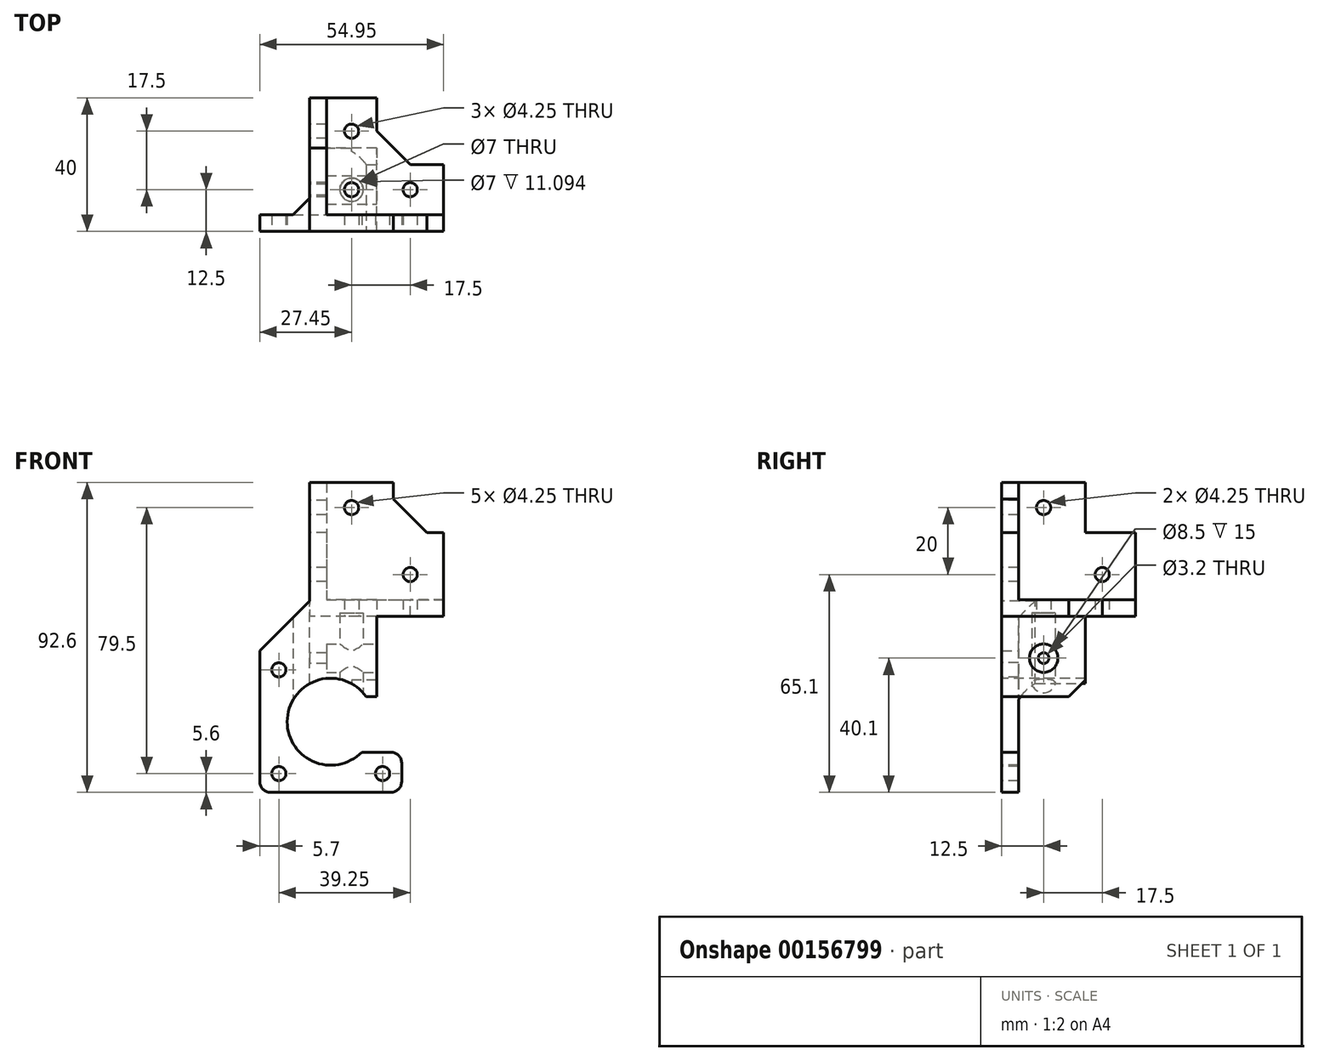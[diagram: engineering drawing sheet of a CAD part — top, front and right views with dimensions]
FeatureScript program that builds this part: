
annotation { "Feature Type Name" : "Feature", "Feature Type Description" : "" }
export const myFeature = defineFeature(function(context is Context, id is Id, definition is map)
    precondition{}
    {
        {
            var Q0;
            Q0=qCreatedBy(makeId("Top.planeOp"),FACE);
            var sketch = newSketch(context, id + "F0", { "sketchPlane" : qUnion([Q0])});
            skLineSegment(sketch, "E0", {"start": v(0, 40) * mm, "end": v(-20, 40) * mm});
            skLineSegment(sketch, "E1", {"start": v(-20, 40) * mm, "end": v(-20, 0) * mm});
            skLineSegment(sketch, "E2", {"start": v(-20, 0) * mm, "end": v(20, 0) * mm});
            skLineSegment(sketch, "E3", {"start": v(20, 0) * mm, "end": v(20, 20) * mm});
            skLineSegment(sketch, "E4", {"start": v(20, 20) * mm, "end": v(0, 20) * mm});
            skLineSegment(sketch, "E5", {"start": v(0, 20) * mm, "end": v(0, 40) * mm});
            skCircle(sketch, "E6", {"center": v(-7.5, 30) * mm, "radius": 2.12 * mm});
            skCircle(sketch, "E7", {"center": v(10, 12.5) * mm, "radius": 2.12 * mm});
            skCircle(sketch, "E8", {"center": v(-7.5, 12.5) * mm, "radius": 2.12 * mm});
            skSolve(sketch);
        }
        {
            var Q0;
            Q0=qSketchRegion(id+"F0",true);
            extrude(context, id + "F1", {"entities" : qUnion([Q0]), "depth" : 5 * mm});
        }
        {
            var Q0;
            Q0=makeQuery(id+"F1.opExtrude","CAP_FACE",FACE,{"disambiguationData":[OSD([sQuery(id+"F0.wireOp",EDGE,"E0"),sQuery(id+"F0.wireOp",EDGE,"E1"),sQuery(id+"F0.wireOp",EDGE,"E2"),sQuery(id+"F0.wireOp",EDGE,"E3"),sQuery(id+"F0.wireOp",EDGE,"E4"),sQuery(id+"F0.wireOp",EDGE,"E5"),sQuery(id+"F0.wireOp",EDGE,"E6"),sQuery(id+"F0.wireOp",EDGE,"E7")])],"isStart":false});
            var sketch = newSketch(context, id + "F2", { "sketchPlane" : qUnion([Q0])});
            skLineSegment(sketch, "E9", {"start": v(-20, 40) * mm, "end": v(-15, 40) * mm});
            skLineSegment(sketch, "E10", {"start": v(-15, 40) * mm, "end": v(-15, 5) * mm});
            skLineSegment(sketch, "E11", {"start": v(-15, 5) * mm, "end": v(20, 5) * mm});
            skLineSegment(sketch, "E12", {"start": v(20, 5) * mm, "end": v(20, 0) * mm});
            skLineSegment(sketch, "E13", {"start": v(20, 0) * mm, "end": v(-20, 0) * mm});
            skLineSegment(sketch, "E14", {"start": v(-20, 0) * mm, "end": v(-20, 40) * mm});
            skSolve(sketch);
        }
        {
            var Q0;
            Q0=qSketchRegion(id+"F2",true);
            extrude(context, id + "F3", {"entities" : qUnion([Q0]), "operationType" : NewBodyOperationType.ADD, "depth" : 20 * mm});
        }
        {
            var Q0;
            Q0=makeQuery(id+"F3.opExtrude","CAP_FACE",FACE,{"disambiguationData":[OSD([sQuery(id+"F2.wireOp",EDGE,"E9"),sQuery(id+"F2.wireOp",EDGE,"E10"),sQuery(id+"F2.wireOp",EDGE,"E11"),sQuery(id+"F2.wireOp",EDGE,"E12"),sQuery(id+"F2.wireOp",EDGE,"E13"),sQuery(id+"F2.wireOp",EDGE,"E14")])],"isStart":false});
            var sketch = newSketch(context, id + "F4", { "sketchPlane" : qUnion([Q0])});
            skLineSegment(sketch, "E15", {"start": v(-15, 25) * mm, "end": v(-20, 25) * mm});
            skLineSegment(sketch, "E16", {"start": v(-20, 25) * mm, "end": v(-20, 0) * mm});
            skLineSegment(sketch, "E17", {"start": v(-20, 0) * mm, "end": v(5, 0) * mm});
            skLineSegment(sketch, "E18", {"start": v(5, 0) * mm, "end": v(5, 5) * mm});
            skLineSegment(sketch, "E19", {"start": v(5, 5) * mm, "end": v(-15, 5) * mm});
            skLineSegment(sketch, "E20", {"start": v(-15, 5) * mm, "end": v(-15, 25) * mm});
            skSolve(sketch);
        }
        {
            var Q0;
            Q0=qSketchRegion(id+"F4",true);
            extrude(context, id + "F5", {"entities" : qUnion([Q0]), "operationType" : NewBodyOperationType.ADD, "depth" : 15 * mm});
        }
        {
            var Q0;
            Q0=makeQuery(id+"F1.opExtrude","SWEPT_EDGE",EDGE,{"disambiguationData":[OSD([sQuery(id+"F0.wireOp",EDGE,"E4"),sQuery(id+"F0.wireOp",EDGE,"E5")])]});
            var Q1;
            Q1=makeQuery(id+"F5.opExtrude","CAP_EDGE",EDGE,{"disambiguationData":[OSD([sQuery(id+"F4.wireOp",EDGE,"E15")])],"isStart":true});
            var Q2;
            Q2=makeQuery(id+"F5.opExtrude","CAP_EDGE",EDGE,{"disambiguationData":[OSD([sQuery(id+"F4.wireOp",EDGE,"E18")])],"isStart":true});
            chamfer(context, id + "F6", {"entities" : qUnion([Q0, Q1, Q2]), "width" : 10 * mm, "tangentPropagation" : true});
        }
        {
            var Q0;
            Q0=makeQuery(id+"F5.boolean.opBoolean","MERGE",FACE,{"derivedFrom":[makeQuery(id+"F3.boolean.opBoolean","MERGE",FACE,{"derivedFrom":[makeQuery(id+"F1.opExtrude","SWEPT_FACE",FACE,{"disambiguationData":[OSD([sQuery(id+"F0.wireOp",EDGE,"E2")])]}),makeQuery(id+"F3.opExtrude","SWEPT_FACE",FACE,{"disambiguationData":[OSD([sQuery(id+"F2.wireOp",EDGE,"E13")])]})]}),makeQuery(id+"F5.opExtrude","SWEPT_FACE",FACE,{"disambiguationData":[OSD([sQuery(id+"F4.wireOp",EDGE,"E17")])]})]});
            var sketch = newSketch(context, id + "F7", { "sketchPlane" : qUnion([Q0])});
            skCircle(sketch, "E21", {"center": v(-7.5, 32.5) * mm, "radius": 2.12 * mm});
            skCircle(sketch, "E22", {"center": v(10, 12.5) * mm, "radius": 2.12 * mm});
            skSolve(sketch);
        }
        {
            var Q0;
            Q0=qSketchRegion(id+"F7",true);
            extrude(context, id + "F8", {"entities" : qUnion([Q0]), "operationType" : NewBodyOperationType.REMOVE, "oppositeDirection" : true, "depth" : 5 * mm});
        }
        {
            var Q0;
            Q0=makeQuery(id+"F5.boolean.opBoolean","MERGE",FACE,{"derivedFrom":[makeQuery(id+"F3.boolean.opBoolean","MERGE",FACE,{"derivedFrom":[makeQuery(id+"F1.opExtrude","SWEPT_FACE",FACE,{"disambiguationData":[OSD([sQuery(id+"F0.wireOp",EDGE,"E1")])]}),makeQuery(id+"F3.opExtrude","SWEPT_FACE",FACE,{"disambiguationData":[OSD([sQuery(id+"F2.wireOp",EDGE,"E14")])]})]}),makeQuery(id+"F5.opExtrude","SWEPT_FACE",FACE,{"disambiguationData":[OSD([sQuery(id+"F4.wireOp",EDGE,"E16")])]})]});
            var sketch = newSketch(context, id + "F9", { "sketchPlane" : qUnion([Q0])});
            skCircle(sketch, "E23", {"center": v(-12.5, 32.5) * mm, "radius": 2.12 * mm});
            skCircle(sketch, "E24", {"center": v(-30, 12.5) * mm, "radius": 2.12 * mm});
            skSolve(sketch);
        }
        {
            var Q0;
            Q0=qSketchRegion(id+"F9",true);
            extrude(context, id + "F10", {"entities" : qUnion([Q0]), "operationType" : NewBodyOperationType.REMOVE, "oppositeDirection" : true, "depth" : 5 * mm});
        }
        {
            var Q0;
            Q0=makeQuery(id+"F1.opExtrude","CAP_FACE",FACE,{"disambiguationData":[OSD([sQuery(id+"F0.wireOp",EDGE,"E0"),sQuery(id+"F0.wireOp",EDGE,"E1"),sQuery(id+"F0.wireOp",EDGE,"E2"),sQuery(id+"F0.wireOp",EDGE,"E3"),sQuery(id+"F0.wireOp",EDGE,"E4"),sQuery(id+"F0.wireOp",EDGE,"E5"),sQuery(id+"F0.wireOp",EDGE,"E6"),sQuery(id+"F0.wireOp",EDGE,"E7"),sQuery(id+"F0.wireOp",EDGE,"E8")])],"isStart":true});
            var sketch = newSketch(context, id + "F11", { "sketchPlane" : qUnion([Q0])});
            skLineSegment(sketch, "E25.bottom", {"start": v(20, -20) * mm, "end": v(-20, -20) * mm});
            skLineSegment(sketch, "E25.top", {"start": v(20, 0) * mm, "end": v(-20, 0) * mm});
            skLineSegment(sketch, "E25.left", {"start": v(20, -20) * mm, "end": v(20, 0) * mm});
            skLineSegment(sketch, "E25.right", {"start": v(-20, -20) * mm, "end": v(-20, 0) * mm});
            skPoint(sketch, "E25.middle", {"position": v(0, -10) * mm});
            skPoint(sketch, "E26.visualSharp", {"position": v(-20, 0) * mm});
            skLineSegment(sketch, "E26.filletArc", {"start": v(-20, 0) * mm, "end": v(-20, 0) * mm});
            skCircle(sketch, "E27", {"center": v(10, -12.5) * mm, "radius": 2.12 * mm});
            skCircle(sketch, "E28", {"center": v(-7.5, -12.5) * mm, "radius": 2.12 * mm});
            skSolve(sketch);
        }
        {
            var Q0;
            Q0=qSketchRegion(id+"F11",true);
            extrude(context, id + "F12", {"entities" : qUnion([Q0]), "operationType" : NewBodyOperationType.ADD, "depth" : 24 * mm});
        }
        {
            var Q0;
            Q0=makeQuery(id+"F12.boolean.opBoolean","MERGE",FACE,{"derivedFrom":[makeQuery(id+"F1.opExtrude","SWEPT_FACE",FACE,{"disambiguationData":[OSD([sQuery(id+"F0.wireOp",EDGE,"E4")])]}),makeQuery(id+"F12.opExtrude","SWEPT_FACE",FACE,{"disambiguationData":[OSD([sQuery(id+"F11.wireOp",EDGE,"E25.bottom")])]})]});
            var sketch = newSketch(context, id + "F13", { "sketchPlane" : qUnion([Q0])});
            skLineSegment(sketch, "E29", {"start": v(20, -11.5) * mm, "end": v(20, -24) * mm});
            skLineSegment(sketch, "E30", {"start": v(20, -24) * mm, "end": v(7.5, -24) * mm});
            skPoint(sketch, "E31.orphan", {"position": v(7.5, -24) * mm});
            skCircle(sketch, "E32", {"center": v(7.5, -11.5) * mm, "radius": 4.15 * mm, "construction": true});
            skLineSegment(sketch, "E33", {"start": v(0, -11.5) * mm, "end": v(0, 0) * mm});
            skLineSegment(sketch, "E34", {"start": v(0, 0) * mm, "end": v(-20, 0) * mm});
            skLineSegment(sketch, "E35", {"start": v(-20, 0) * mm, "end": v(-20, -24) * mm});
            skLineSegment(sketch, "E36", {"start": v(-20, -24) * mm, "end": v(7.5, -24) * mm});
            skLineSegment(sketch, "E37", {"start": v(0, -11.5) * mm, "end": v(0, -24) * mm});
            skSolve(sketch);
        }
        {
            var Q0;
            Q0=qSketchRegion(id+"F13",true);
            extrude(context, id + "F14", {"entities" : qUnion([Q0]), "operationType" : NewBodyOperationType.REMOVE, "oppositeDirection" : true, "depth" : 25 * mm});
        }
        {
            var Q0;
            Q0=makeQuery(id+"F14.boolean.opBoolean","COPY",FACE,{"derivedFrom":makeQuery(id+"F14.opExtrude","SWEPT_FACE",FACE,{"disambiguationData":[OSD([sQuery(id+"F13.wireOp",EDGE,"E33"),sQuery(id+"F13.wireOp",EDGE,"E37")])]})});
            var sketch = newSketch(context, id + "F15", { "sketchPlane" : qUnion([Q0])});
            skCircle(sketch, "E38", {"center": v(12.5, -12.5) * mm, "radius": 4.25 * mm});
            skSolve(sketch);
        }
        {
            var Q0;
            Q0=qSketchRegion(id+"F15",true);
            extrude(context, id + "F16", {"entities" : qUnion([Q0]), "operationType" : NewBodyOperationType.REMOVE, "oppositeDirection" : true, "depth" : 20 * mm});
        }
        {
            var Q0;
            Q0=makeQuery(id+"F12.opExtrude","CAP_FACE",FACE,{"disambiguationData":[OSD([sQuery(id+"F11.wireOp",EDGE,"E25.bottom"),sQuery(id+"F11.wireOp",EDGE,"E25.top"),sQuery(id+"F11.wireOp",EDGE,"E25.left"),sQuery(id+"F11.wireOp",EDGE,"E25.right"),sQuery(id+"F11.wireOp",EDGE,"E27"),sQuery(id+"F11.wireOp",EDGE,"E28")])],"isStart":false});
            var sketch = newSketch(context, id + "F17", { "sketchPlane" : qUnion([Q0])});
            skCircle(sketch, "E39", {"center": v(-7.5, -12.5) * mm, "radius": 3.5 * mm});
            skSolve(sketch);
        }
        {
            var Q0;
            Q0=qSketchRegion(id+"F17",true);
            extrude(context, id + "F18", {"entities" : qUnion([Q0]), "operationType" : NewBodyOperationType.REMOVE, "oppositeDirection" : true, "depth" : 25 * mm});
        }
        {
            var Q0;
            {var subQ1=sQuery(id+"F11.wireOp",EDGE,"E25.bottom");var subQ2=sQuery(id+"F0.wireOp",EDGE,"E1");var subQ3=sQuery(id+"F0.wireOp",EDGE,"E4");Q0=makeQuery(id+"F14.boolean.opBoolean","SPLIT",FACE,{"disambiguationData":[TD([makeQuery(id+"F1.opExtrude","SWEPT_FACE",FACE,{"disambiguationData":[OSD([subQ2])]})])],"derivedFrom":makeQuery(id+"F12.boolean.opBoolean","MERGE",FACE,{"derivedFrom":[makeQuery(id+"F1.opExtrude","SWEPT_FACE",FACE,{"disambiguationData":[OSD([subQ3])]}),makeQuery(id+"F12.opExtrude","SWEPT_FACE",FACE,{"disambiguationData":[OSD([subQ1])]})]})});}
            var sketch = newSketch(context, id + "F19", { "sketchPlane" : qUnion([Q0])});
            skLineSegment(sketch, "E40.bottom", {"start": v(0, 0) * mm, "end": v(20, 0) * mm});
            skLineSegment(sketch, "E40.top", {"start": v(0, -24) * mm, "end": v(20, -24) * mm});
            skLineSegment(sketch, "E40.left", {"start": v(0, 0) * mm, "end": v(0, -24) * mm});
            skLineSegment(sketch, "E40.right", {"start": v(20, 0) * mm, "end": v(20, -24) * mm});
            skSolve(sketch);
        }
        {
            var Q0;
            Q0=qSketchRegion(id+"F19",true);
            extrude(context, id + "F20", {"entities" : qUnion([Q0]), "operationType" : NewBodyOperationType.ADD, "depth" : 5 * mm});
        }
        {
            var Q0;
            Q0=makeQuery(id+"F20.boolean.opBoolean","MERGE",FACE,{"derivedFrom":[makeQuery(id+"F12.boolean.opBoolean","MERGE",FACE,{"derivedFrom":[makeQuery(id+"F5.boolean.opBoolean","MERGE",FACE,{"derivedFrom":[makeQuery(id+"F3.boolean.opBoolean","MERGE",FACE,{"derivedFrom":[makeQuery(id+"F1.opExtrude","SWEPT_FACE",FACE,{"disambiguationData":[OSD([sQuery(id+"F0.wireOp",EDGE,"E1")])]}),makeQuery(id+"F3.opExtrude","SWEPT_FACE",FACE,{"disambiguationData":[OSD([sQuery(id+"F2.wireOp",EDGE,"E14")])]})]}),makeQuery(id+"F5.opExtrude","SWEPT_FACE",FACE,{"disambiguationData":[OSD([sQuery(id+"F4.wireOp",EDGE,"E16")])]})]}),makeQuery(id+"F12.opExtrude","SWEPT_FACE",FACE,{"disambiguationData":[OSD([sQuery(id+"F11.wireOp",EDGE,"E25.right")])]})]}),makeQuery(id+"F20.opExtrude","SWEPT_FACE",FACE,{"disambiguationData":[OSD([sQuery(id+"F19.wireOp",EDGE,"E40.right")])]})]});
            var sketch = newSketch(context, id + "F21", { "sketchPlane" : qUnion([Q0])});
            skLineSegment(sketch, "E41", {"start": v(-25, -24) * mm, "end": v(-25, -44) * mm});
            skLineSegment(sketch, "E42", {"start": v(-25, -44) * mm, "end": v(0, -44) * mm});
            skLineSegment(sketch, "E43", {"start": v(0, -44) * mm, "end": v(0, -24) * mm});
            skLineSegment(sketch, "E44", {"start": v(0, -24) * mm, "end": v(-7.75, -24) * mm});
            skLineSegment(sketch, "E45", {"start": v(-7.75, -24) * mm, "end": v(-7.75, -39) * mm});
            skLineSegment(sketch, "E46", {"start": v(-7.75, -39) * mm, "end": v(-17.25, -39) * mm});
            skLineSegment(sketch, "E47", {"start": v(-17.25, -39) * mm, "end": v(-17.25, -24) * mm});
            skLineSegment(sketch, "E48", {"start": v(-17.25, -24) * mm, "end": v(-25, -24) * mm});
            skSolve(sketch);
        }
        {
            var Q0;
            Q0=qSketchRegion(id+"F21",true);
            extrude(context, id + "F22", {"entities" : qUnion([Q0]), "operationType" : NewBodyOperationType.ADD, "oppositeDirection" : true, "depth" : 12.5 * mm});
        }
        {
            var Q0;
            Q0=makeQuery(id+"F22.opExtrude","SWEPT_EDGE",EDGE,{"disambiguationData":[OSD([sQuery(id+"F21.wireOp",EDGE,"E41"),sQuery(id+"F21.wireOp",EDGE,"E42")])]});
            var Q1;
            Q1=makeQuery(id+"F22.opExtrude","SWEPT_EDGE",EDGE,{"disambiguationData":[OSD([sQuery(id+"F21.wireOp",EDGE,"E42"),sQuery(id+"F21.wireOp",EDGE,"E43")])]});
            var Q2;
            Q2=makeQuery(id+"F12.opExtrude","CAP_EDGE",EDGE,{"disambiguationData":[OSD([sQuery(id+"F11.wireOp",EDGE,"E25.top")])],"isStart":false});
            var Q3;
            Q3=makeQuery(id+"F20.opExtrude","CAP_EDGE",EDGE,{"disambiguationData":[OSD([sQuery(id+"F19.wireOp",EDGE,"E40.top")])],"isStart":false});
            var Q4;
            Q4=makeQuery(id+"F20.opExtrude","CAP_EDGE",EDGE,{"disambiguationData":[OSD([sQuery(id+"F19.wireOp",EDGE,"E40.bottom")])],"isStart":false});
            chamfer(context, id + "F23", {"entities" : qUnion([Q0, Q1, Q2, Q3, Q4]), "width" : 5 * mm, "tangentPropagation" : true});
        }
        {
            var Q0;
            Q0=makeQuery(id+"F23.opChamfer","SPLIT",FACE,{"disambiguationData":[OD(1.0)],"derivedFrom":makeQuery(id+"F14.boolean.opBoolean","MERGE",FACE,{"derivedFrom":[makeQuery(id+"F1.opExtrude","CAP_FACE",FACE,{"disambiguationData":[OSD([sQuery(id+"F0.wireOp",EDGE,"E0"),sQuery(id+"F0.wireOp",EDGE,"E1"),sQuery(id+"F0.wireOp",EDGE,"E2"),sQuery(id+"F0.wireOp",EDGE,"E3"),sQuery(id+"F0.wireOp",EDGE,"E4"),sQuery(id+"F0.wireOp",EDGE,"E5"),sQuery(id+"F0.wireOp",EDGE,"E6"),sQuery(id+"F0.wireOp",EDGE,"E7"),sQuery(id+"F0.wireOp",EDGE,"E8")])],"isStart":true}),makeQuery(id+"F14.opExtrude","SWEPT_FACE",FACE,{"disambiguationData":[OSD([sQuery(id+"F13.wireOp",EDGE,"E34")])]})]})});
            var sketch = newSketch(context, id + "F24", { "sketchPlane" : qUnion([Q0])});
            skCircle(sketch, "E49", {"center": v(-7.5, -30) * mm, "radius": 3.5 * mm});
            skSolve(sketch);
        }
        {
            var Q0;
            Q0=qSketchRegion(id+"F24",true);
            extrude(context, id + "F25", {"entities" : qUnion([Q0]), "operationType" : NewBodyOperationType.REMOVE, "endBound" : BoundingType.THROUGH_ALL, "depth" : 25 * mm});
        }
        {
            var Q0;
            Q0=makeQuery(id+"F22.boolean.opBoolean","MERGE",FACE,{"derivedFrom":[makeQuery(id+"F20.boolean.opBoolean","MERGE",FACE,{"derivedFrom":[makeQuery(id+"F12.boolean.opBoolean","MERGE",FACE,{"derivedFrom":[makeQuery(id+"F5.boolean.opBoolean","MERGE",FACE,{"derivedFrom":[makeQuery(id+"F3.boolean.opBoolean","MERGE",FACE,{"derivedFrom":[makeQuery(id+"F1.opExtrude","SWEPT_FACE",FACE,{"disambiguationData":[OSD([sQuery(id+"F0.wireOp",EDGE,"E1")])]}),makeQuery(id+"F3.opExtrude","SWEPT_FACE",FACE,{"disambiguationData":[OSD([sQuery(id+"F2.wireOp",EDGE,"E14")])]})]}),makeQuery(id+"F5.opExtrude","SWEPT_FACE",FACE,{"disambiguationData":[OSD([sQuery(id+"F4.wireOp",EDGE,"E16")])]})]}),makeQuery(id+"F12.opExtrude","SWEPT_FACE",FACE,{"disambiguationData":[OSD([sQuery(id+"F11.wireOp",EDGE,"E25.right")])]})]}),makeQuery(id+"F20.opExtrude","SWEPT_FACE",FACE,{"disambiguationData":[OSD([sQuery(id+"F19.wireOp",EDGE,"E40.right")])]})]}),makeQuery(id+"F22.opExtrude","CAP_FACE",FACE,{"disambiguationData":[OSD([sQuery(id+"F21.wireOp",EDGE,"E41"),sQuery(id+"F21.wireOp",EDGE,"E42"),sQuery(id+"F21.wireOp",EDGE,"E43"),sQuery(id+"F21.wireOp",EDGE,"E44"),sQuery(id+"F21.wireOp",EDGE,"E45"),sQuery(id+"F21.wireOp",EDGE,"E46"),sQuery(id+"F21.wireOp",EDGE,"E47"),sQuery(id+"F21.wireOp",EDGE,"E48")])],"isStart":true})]});
            var sketch = newSketch(context, id + "F26", { "sketchPlane" : qUnion([Q0])});
            skCircle(sketch, "E50", {"center": v(-12.5, -12.5) * mm, "radius": 4.25 * mm});
            skCircle(sketch, "E51", {"center": v(-12.5, -12.5) * mm, "radius": 1.6 * mm});
            skSolve(sketch);
        }
        {
            var Q0;
            Q0=qSketchRegion(id+"F26",true);
            extrude(context, id + "F27", {"entities" : qUnion([Q0]), "operationType" : NewBodyOperationType.ADD, "oppositeDirection" : true, "depth" : 5 * mm});
        }
        {
            var Q0;
            Q0=makeQuery(id+"F22.boolean.opBoolean","MERGE",FACE,{"derivedFrom":[makeQuery(id+"F12.boolean.opBoolean","MERGE",FACE,{"derivedFrom":[makeQuery(id+"F5.boolean.opBoolean","MERGE",FACE,{"derivedFrom":[makeQuery(id+"F3.boolean.opBoolean","MERGE",FACE,{"derivedFrom":[makeQuery(id+"F1.opExtrude","SWEPT_FACE",FACE,{"disambiguationData":[OSD([sQuery(id+"F0.wireOp",EDGE,"E2")])]}),makeQuery(id+"F3.opExtrude","SWEPT_FACE",FACE,{"disambiguationData":[OSD([sQuery(id+"F2.wireOp",EDGE,"E13")])]})]}),makeQuery(id+"F5.opExtrude","SWEPT_FACE",FACE,{"disambiguationData":[OSD([sQuery(id+"F4.wireOp",EDGE,"E17")])]})]}),makeQuery(id+"F12.opExtrude","SWEPT_FACE",FACE,{"disambiguationData":[OSD([sQuery(id+"F11.wireOp",EDGE,"E25.top")])]})]}),makeQuery(id+"F22.opExtrude","SWEPT_FACE",FACE,{"disambiguationData":[OSD([sQuery(id+"F21.wireOp",EDGE,"E43")])]})]});
            var sketch = newSketch(context, id + "F28", { "sketchPlane" : qUnion([Q0])});
            skCircle(sketch, "E52", {"center": v(-13.75, -31.5) * mm, "radius": 2.12 * mm});
            skSolve(sketch);
        }
        {
            var Q0;
            Q0=qSketchRegion(id+"F28",true);
            extrude(context, id + "F29", {"entities" : qUnion([Q0]), "operationType" : NewBodyOperationType.REMOVE, "endBound" : BoundingType.THROUGH_ALL, "oppositeDirection" : true, "depth" : 25 * mm});
        }
        {
            var Q0;
            Q0=makeQuery(id+"F22.boolean.opBoolean","MERGE",FACE,{"derivedFrom":[makeQuery(id+"F12.boolean.opBoolean","MERGE",FACE,{"derivedFrom":[makeQuery(id+"F5.boolean.opBoolean","MERGE",FACE,{"derivedFrom":[makeQuery(id+"F3.boolean.opBoolean","MERGE",FACE,{"derivedFrom":[makeQuery(id+"F1.opExtrude","SWEPT_FACE",FACE,{"disambiguationData":[OSD([sQuery(id+"F0.wireOp",EDGE,"E2")])]}),makeQuery(id+"F3.opExtrude","SWEPT_FACE",FACE,{"disambiguationData":[OSD([sQuery(id+"F2.wireOp",EDGE,"E13")])]})]}),makeQuery(id+"F5.opExtrude","SWEPT_FACE",FACE,{"disambiguationData":[OSD([sQuery(id+"F4.wireOp",EDGE,"E17")])]})]}),makeQuery(id+"F12.opExtrude","SWEPT_FACE",FACE,{"disambiguationData":[OSD([sQuery(id+"F11.wireOp",EDGE,"E25.top")])]})]}),makeQuery(id+"F22.opExtrude","SWEPT_FACE",FACE,{"disambiguationData":[OSD([sQuery(id+"F21.wireOp",EDGE,"E43")])]})]});
            var sketch = newSketch(context, id + "F30", { "sketchPlane" : qUnion([Q0])});
            skCircle(sketch, "E53.cCircle", {"center": v(-13.75, -31.5) * mm, "radius": 2.93 * mm, "construction": true});
            skLineSegment(sketch, "E53.0", {"start": v(-10.82, -29.81) * mm, "end": v(-10.82, -33.19) * mm});
            skLineSegment(sketch, "E53.1", {"start": v(-10.82, -33.19) * mm, "end": v(-13.75, -34.88) * mm});
            skLineSegment(sketch, "E53.2", {"start": v(-13.75, -34.88) * mm, "end": v(-16.67, -33.19) * mm});
            skLineSegment(sketch, "E53.3", {"start": v(-16.67, -33.19) * mm, "end": v(-16.67, -29.81) * mm});
            skLineSegment(sketch, "E53.4", {"start": v(-16.67, -29.81) * mm, "end": v(-13.75, -28.12) * mm});
            skLineSegment(sketch, "E53.5", {"start": v(-13.75, -28.12) * mm, "end": v(-10.82, -29.81) * mm});
            skPoint(sketch, "E53.0.midPoint", {"position": v(-10.82, -31.5) * mm});
            skPoint(sketch, "E54.0.midPoint", {"position": v(-7.5, -31.5) * mm});
            skSolve(sketch);
        }
        {
            var Q0;
            Q0=qSketchRegion(id+"F30",true);
            extrude(context, id + "F31", {"entities" : qUnion([Q0]), "operationType" : NewBodyOperationType.REMOVE, "oppositeDirection" : true, "depth" : 4 * mm});
        }
        {
            var Q0;
            Q0=makeQuery(id+"F22.boolean.opBoolean","MERGE",FACE,{"derivedFrom":[makeQuery(id+"F20.opExtrude","CAP_FACE",FACE,{"disambiguationData":[OSD([sQuery(id+"F19.wireOp",EDGE,"E40.bottom"),sQuery(id+"F19.wireOp",EDGE,"E40.top"),sQuery(id+"F19.wireOp",EDGE,"E40.left"),sQuery(id+"F19.wireOp",EDGE,"E40.right")])],"isStart":false}),makeQuery(id+"F22.opExtrude","SWEPT_FACE",FACE,{"disambiguationData":[OSD([sQuery(id+"F21.wireOp",EDGE,"E41")])]})]});
            var sketch = newSketch(context, id + "F32", { "sketchPlane" : qUnion([Q0])});
            skCircle(sketch, "E55", {"center": v(13.75, -31.5) * mm, "radius": 3.5 * mm});
            skSolve(sketch);
        }
        {
            var Q0;
            Q0=qSketchRegion(id+"F32",true);
            extrude(context, id + "F33", {"entities" : qUnion([Q0]), "operationType" : NewBodyOperationType.REMOVE, "oppositeDirection" : true, "depth" : 4 * mm});
        }
        {
            var Q0;
            Q0=makeQuery(id+"F22.boolean.opBoolean","MERGE",FACE,{"derivedFrom":[makeQuery(id+"F12.boolean.opBoolean","MERGE",FACE,{"derivedFrom":[makeQuery(id+"F5.boolean.opBoolean","MERGE",FACE,{"derivedFrom":[makeQuery(id+"F3.boolean.opBoolean","MERGE",FACE,{"derivedFrom":[makeQuery(id+"F1.opExtrude","SWEPT_FACE",FACE,{"disambiguationData":[OSD([sQuery(id+"F0.wireOp",EDGE,"E2")])]}),makeQuery(id+"F3.opExtrude","SWEPT_FACE",FACE,{"disambiguationData":[OSD([sQuery(id+"F2.wireOp",EDGE,"E13")])]})]}),makeQuery(id+"F5.opExtrude","SWEPT_FACE",FACE,{"disambiguationData":[OSD([sQuery(id+"F4.wireOp",EDGE,"E17")])]})]}),makeQuery(id+"F12.opExtrude","SWEPT_FACE",FACE,{"disambiguationData":[OSD([sQuery(id+"F11.wireOp",EDGE,"E25.top")])]})]}),makeQuery(id+"F22.opExtrude","SWEPT_FACE",FACE,{"disambiguationData":[OSD([sQuery(id+"F21.wireOp",EDGE,"E43")])]})]});
            var sketch = newSketch(context, id + "F34", { "sketchPlane" : qUnion([Q0])});
            skLineSegment(sketch, "E56.bottom", {"start": v(-7.5, -44) * mm, "end": v(-20, -44) * mm});
            skLineSegment(sketch, "E56.top", {"start": v(-7.5, -24) * mm, "end": v(-20, -24) * mm});
            skLineSegment(sketch, "E56.left", {"start": v(-7.5, -44) * mm, "end": v(-7.5, -24) * mm});
            skLineSegment(sketch, "E56.right", {"start": v(-20, -44) * mm, "end": v(-20, -24) * mm});
            skPoint(sketch, "E56.middle", {"position": v(-13.75, -34) * mm});
            skSolve(sketch);
        }
        {
            var Q0;
            Q0 = qSketchRegion(id + "F34", true);
            extrude(context, id + "F35", {"entities" : qUnion([Q0]), "operationType" : NewBodyOperationType.REMOVE, "endBound" : BoundingType.THROUGH_ALL, "oppositeDirection" : true, "depth" : 25 * mm});
        }
        {
            var Q0;
            Q0=makeQuery(id+"F22.boolean.opBoolean","MERGE",FACE,{"derivedFrom":[makeQuery(id+"F12.boolean.opBoolean","MERGE",FACE,{"derivedFrom":[makeQuery(id+"F5.boolean.opBoolean","MERGE",FACE,{"derivedFrom":[makeQuery(id+"F3.boolean.opBoolean","MERGE",FACE,{"derivedFrom":[makeQuery(id+"F1.opExtrude","SWEPT_FACE",FACE,{"disambiguationData":[OSD([sQuery(id+"F0.wireOp",EDGE,"E2")])]}),makeQuery(id+"F3.opExtrude","SWEPT_FACE",FACE,{"disambiguationData":[OSD([sQuery(id+"F2.wireOp",EDGE,"E13")])]})]}),makeQuery(id+"F5.opExtrude","SWEPT_FACE",FACE,{"disambiguationData":[OSD([sQuery(id+"F4.wireOp",EDGE,"E17")])]})]}),makeQuery(id+"F12.opExtrude","SWEPT_FACE",FACE,{"disambiguationData":[OSD([sQuery(id+"F11.wireOp",EDGE,"E25.top")])]})]}),makeQuery(id+"F22.opExtrude","SWEPT_FACE",FACE,{"disambiguationData":[OSD([sQuery(id+"F21.wireOp",EDGE,"E43")])]})]});
            var sketch = newSketch(context, id + "F36", { "sketchPlane" : qUnion([Q0])});
            skArc(sketch, "E57", {"start": v(-3.13, -24) * mm, "mid": v(-26.7, -30.46) * mm, "end": v(-4.47, -40.6) * mm});
            skLineSegment(sketch, "E58.bottom", {"start": v(1.75, -47) * mm, "end": v(-29.25, -47) * mm, "construction": true});
            skLineSegment(sketch, "E58.top", {"start": v(1.75, -16) * mm, "end": v(-29.25, -16) * mm, "construction": true});
            skLineSegment(sketch, "E58.left", {"start": v(1.75, -47) * mm, "end": v(1.75, -16) * mm, "construction": true});
            skLineSegment(sketch, "E58.right", {"start": v(-29.25, -47) * mm, "end": v(-29.25, -16) * mm, "construction": true});
            skCircle(sketch, "E59", {"center": v(-29.25, -16) * mm, "radius": 2.12 * mm});
            skCircle(sketch, "E60", {"center": v(1.75, -16) * mm, "radius": 2.12 * mm, "construction": true});
            skCircle(sketch, "E61", {"center": v(1.75, -47) * mm, "radius": 2.12 * mm});
            skCircle(sketch, "E62", {"center": v(-29.25, -47) * mm, "radius": 2.12 * mm});
            skLineSegment(sketch, "E63.bottom", {"start": v(7.45, -52.6) * mm, "end": v(-34.95, -52.6) * mm});
            skLineSegment(sketch, "E63.top", {"start": v(0, -10.4) * mm, "end": v(-34.95, -10.4) * mm});
            skLineSegment(sketch, "E63.left", {"start": v(7.45, -52.6) * mm, "end": v(7.45, -40.6) * mm});
            skLineSegment(sketch, "E63.right", {"start": v(-34.95, -52.6) * mm, "end": v(-34.95, -10.4) * mm});
            skLineSegment(sketch, "E64", {"start": v(-3.13, -24) * mm, "end": v(0, -24) * mm});
            skLineSegment(sketch, "E65", {"start": v(0, -10.4) * mm, "end": v(0, -24) * mm});
            skLineSegment(sketch, "E66", {"start": v(-4.47, -40.6) * mm, "end": v(7.45, -40.6) * mm});
            skPoint(sketch, "E67.orphan", {"position": v(7.45, -10.4) * mm});
            skSolve(sketch);
        }
        {
            var Q0;
            Q0 = qSketchRegion(id + "F36", true);
            extrude(context, id + "F37", {"entities" : qUnion([Q0]), "operationType" : NewBodyOperationType.ADD, "oppositeDirection" : true, "depth" : 5 * mm});
        }
        {
            var Q0;
            Q0=makeQuery(id+"F37.opExtrude","CAP_FACE",FACE,{"disambiguationData":[OSD([sQuery(id+"F36.wireOp",EDGE,"E57"),sQuery(id+"F36.wireOp",EDGE,"E59"),sQuery(id+"F36.wireOp",EDGE,"E61"),sQuery(id+"F36.wireOp",EDGE,"E62"),sQuery(id+"F36.wireOp",EDGE,"E63.bottom"),sQuery(id+"F36.wireOp",EDGE,"E63.top"),sQuery(id+"F36.wireOp",EDGE,"E63.left"),sQuery(id+"F36.wireOp",EDGE,"E63.right"),sQuery(id+"F36.wireOp",EDGE,"E64"),sQuery(id+"F36.wireOp",EDGE,"E65"),sQuery(id+"F36.wireOp",EDGE,"E66")])],"isStart":false});
            var sketch = newSketch(context, id + "F38", { "sketchPlane" : qUnion([Q0])});
            skCircle(sketch, "E68", {"center": v(13.75, -31.5) * mm, "radius": 13 * mm});
            skSolve(sketch);
        }
        {
            var Q0;
            Q0 = qSketchRegion(id + "F38", true);
            extrude(context, id + "F39", {"entities" : qUnion([Q0]), "operationType" : NewBodyOperationType.REMOVE, "endBound" : BoundingType.SYMMETRIC, "oppositeDirection" : true, "depth" : 80 * mm});
        }
        {
            var Q0;
            Q0=makeQuery(id+"F37.boolean.opBoolean","INTERSECT",EDGE,{"derivedFrom":[makeQuery(id+"F27.boolean.opBoolean","MERGE",FACE,{"derivedFrom":[makeQuery(id+"F22.boolean.opBoolean","MERGE",FACE,{"derivedFrom":[makeQuery(id+"F20.boolean.opBoolean","MERGE",FACE,{"derivedFrom":[makeQuery(id+"F12.boolean.opBoolean","MERGE",FACE,{"derivedFrom":[makeQuery(id+"F5.boolean.opBoolean","MERGE",FACE,{"derivedFrom":[makeQuery(id+"F3.boolean.opBoolean","MERGE",FACE,{"derivedFrom":[makeQuery(id+"F1.opExtrude","SWEPT_FACE",FACE,{"disambiguationData":[OSD([sQuery(id+"F0.wireOp",EDGE,"E1")])]}),makeQuery(id+"F3.opExtrude","SWEPT_FACE",FACE,{"disambiguationData":[OSD([sQuery(id+"F2.wireOp",EDGE,"E14")])]})]}),makeQuery(id+"F5.opExtrude","SWEPT_FACE",FACE,{"disambiguationData":[OSD([sQuery(id+"F4.wireOp",EDGE,"E16")])]})]}),makeQuery(id+"F12.opExtrude","SWEPT_FACE",FACE,{"disambiguationData":[OSD([sQuery(id+"F11.wireOp",EDGE,"E25.right")])]})]}),makeQuery(id+"F20.opExtrude","SWEPT_FACE",FACE,{"disambiguationData":[OSD([sQuery(id+"F19.wireOp",EDGE,"E40.right")])]})]}),makeQuery(id+"F22.opExtrude","CAP_FACE",FACE,{"disambiguationData":[OSD([sQuery(id+"F21.wireOp",EDGE,"E41"),sQuery(id+"F21.wireOp",EDGE,"E42"),sQuery(id+"F21.wireOp",EDGE,"E43"),sQuery(id+"F21.wireOp",EDGE,"E44"),sQuery(id+"F21.wireOp",EDGE,"E45"),sQuery(id+"F21.wireOp",EDGE,"E46"),sQuery(id+"F21.wireOp",EDGE,"E47"),sQuery(id+"F21.wireOp",EDGE,"E48")])],"isStart":true})]}),makeQuery(id+"F27.opExtrude","CAP_FACE",FACE,{"disambiguationData":[OSD([sQuery(id+"F26.wireOp",EDGE,"E50"),sQuery(id+"F26.wireOp",EDGE,"E51")])],"isStart":true})]}),makeQuery(id+"F37.opExtrude","SWEPT_FACE",FACE,{"disambiguationData":[OSD([sQuery(id+"F36.wireOp",EDGE,"E63.top")])]})]});
            chamfer(context, id + "F40", {"entities" : qUnion([Q0]), "width" : 15 * mm, "tangentPropagation" : true});
        }
        {
            var Q0;
            Q0=makeQuery(id+"F37.boolean.opBoolean","INTERSECT",EDGE,{"derivedFrom":[makeQuery(id+"F27.boolean.opBoolean","MERGE",FACE,{"derivedFrom":[makeQuery(id+"F22.boolean.opBoolean","MERGE",FACE,{"derivedFrom":[makeQuery(id+"F20.boolean.opBoolean","MERGE",FACE,{"derivedFrom":[makeQuery(id+"F12.boolean.opBoolean","MERGE",FACE,{"derivedFrom":[makeQuery(id+"F5.boolean.opBoolean","MERGE",FACE,{"derivedFrom":[makeQuery(id+"F3.boolean.opBoolean","MERGE",FACE,{"derivedFrom":[makeQuery(id+"F1.opExtrude","SWEPT_FACE",FACE,{"disambiguationData":[OSD([sQuery(id+"F0.wireOp",EDGE,"E1")])]}),makeQuery(id+"F3.opExtrude","SWEPT_FACE",FACE,{"disambiguationData":[OSD([sQuery(id+"F2.wireOp",EDGE,"E14")])]})]}),makeQuery(id+"F5.opExtrude","SWEPT_FACE",FACE,{"disambiguationData":[OSD([sQuery(id+"F4.wireOp",EDGE,"E16")])]})]}),makeQuery(id+"F12.opExtrude","SWEPT_FACE",FACE,{"disambiguationData":[OSD([sQuery(id+"F11.wireOp",EDGE,"E25.right")])]})]}),makeQuery(id+"F20.opExtrude","SWEPT_FACE",FACE,{"disambiguationData":[OSD([sQuery(id+"F19.wireOp",EDGE,"E40.right")])]})]}),makeQuery(id+"F22.opExtrude","CAP_FACE",FACE,{"disambiguationData":[OSD([sQuery(id+"F21.wireOp",EDGE,"E41"),sQuery(id+"F21.wireOp",EDGE,"E42"),sQuery(id+"F21.wireOp",EDGE,"E43"),sQuery(id+"F21.wireOp",EDGE,"E44"),sQuery(id+"F21.wireOp",EDGE,"E45"),sQuery(id+"F21.wireOp",EDGE,"E46"),sQuery(id+"F21.wireOp",EDGE,"E47"),sQuery(id+"F21.wireOp",EDGE,"E48")])],"isStart":true})]}),makeQuery(id+"F27.opExtrude","CAP_FACE",FACE,{"disambiguationData":[OSD([sQuery(id+"F26.wireOp",EDGE,"E50"),sQuery(id+"F26.wireOp",EDGE,"E51")])],"isStart":true})]}),makeQuery(id+"F37.opExtrude","CAP_FACE",FACE,{"disambiguationData":[OSD([sQuery(id+"F36.wireOp",EDGE,"E57"),sQuery(id+"F36.wireOp",EDGE,"E59"),sQuery(id+"F36.wireOp",EDGE,"E61"),sQuery(id+"F36.wireOp",EDGE,"E62"),sQuery(id+"F36.wireOp",EDGE,"E63.bottom"),sQuery(id+"F36.wireOp",EDGE,"E63.top"),sQuery(id+"F36.wireOp",EDGE,"E63.left"),sQuery(id+"F36.wireOp",EDGE,"E63.right"),sQuery(id+"F36.wireOp",EDGE,"E64"),sQuery(id+"F36.wireOp",EDGE,"E65"),sQuery(id+"F36.wireOp",EDGE,"E66")])],"isStart":false})]});
            chamfer(context, id + "F41", {"entities" : qUnion([Q0]), "width" : 5 * mm, "tangentPropagation" : true});
        }
        {
            var Q0;
            Q0=makeQuery(id+"F37.opExtrude","SWEPT_EDGE",EDGE,{"disambiguationData":[OSD([sQuery(id+"F36.wireOp",EDGE,"E63.bottom"),sQuery(id+"F36.wireOp",EDGE,"E63.left")])]});
            var Q1;
            Q1=makeQuery(id+"F37.opExtrude","SWEPT_EDGE",EDGE,{"disambiguationData":[OSD([sQuery(id+"F36.wireOp",EDGE,"E63.bottom"),sQuery(id+"F36.wireOp",EDGE,"E63.right")])]});
            var Q2;
            Q2=makeQuery(id+"F37.opExtrude","SWEPT_EDGE",EDGE,{"disambiguationData":[OSD([sQuery(id+"F36.wireOp",EDGE,"E63.left"),sQuery(id+"F36.wireOp",EDGE,"E66")])]});
            fillet(context, id + "F42", {"entities" : qUnion([Q0, Q1, Q2]), "radius" : 3.2 * mm, "tangentPropagation" : true, "allowEdgeOverflow" : false});
        }
    });
